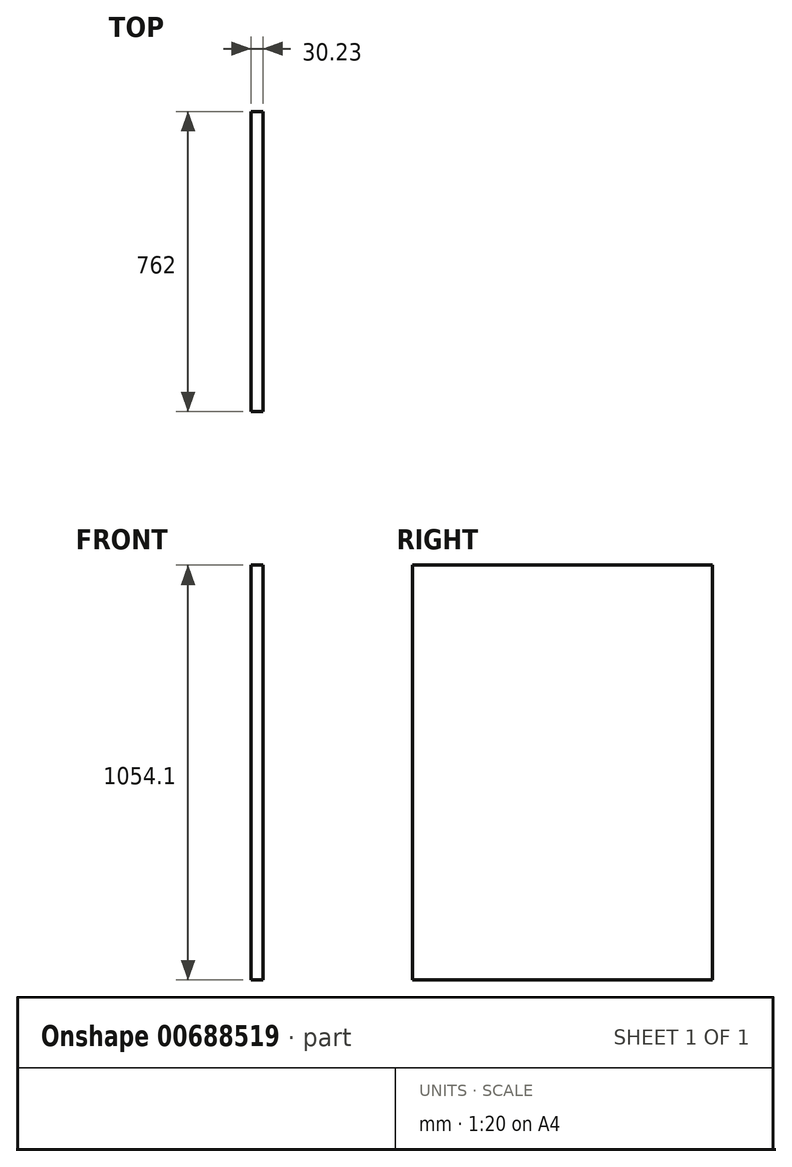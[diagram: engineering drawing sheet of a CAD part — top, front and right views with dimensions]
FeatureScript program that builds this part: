
annotation { "Feature Type Name" : "Feature", "Feature Type Description" : "" }
export const myFeature = defineFeature(function(context is Context, id is Id, definition is map)
    precondition{}
    {
        {
            var Q0;
            Q0=qCreatedBy(makeId("Right.planeOp"),FACE);
            var sketch = newSketch(context, id + "F0", { "sketchPlane" : qUnion([Q0])});
            skLineSegment(sketch, "E0.bottom", {"start": v(381, 527.05) * mm, "end": v(-381, 527.05) * mm});
            skLineSegment(sketch, "E0.top", {"start": v(381, -527.05) * mm, "end": v(-381, -527.05) * mm});
            skLineSegment(sketch, "E0.left", {"start": v(381, 527.05) * mm, "end": v(381, -527.05) * mm});
            skLineSegment(sketch, "E0.right", {"start": v(-381, 527.05) * mm, "end": v(-381, -527.05) * mm});
            skPoint(sketch, "E0.middle", {"position": v(0, 0) * mm});
            skSolve(sketch);
        }
        {
            var Q0;
            Q0=makeQuery(id+"F0.imprint","IMPRINT",FACE,{"disambiguationData":[TD([[makeQuery(id+"F0.imprint","IMPRINT",EDGE,{"derivedFrom":sQuery(id+"F0.wireOp",EDGE,"E0.bottom")}),1.0]])]});
            extrude(context, id + "F1", {"entities" : qUnion([Q0]), "depth" : 30.23 * mm, "offsetDistance" : 25.4 * mm});
        }
    });
